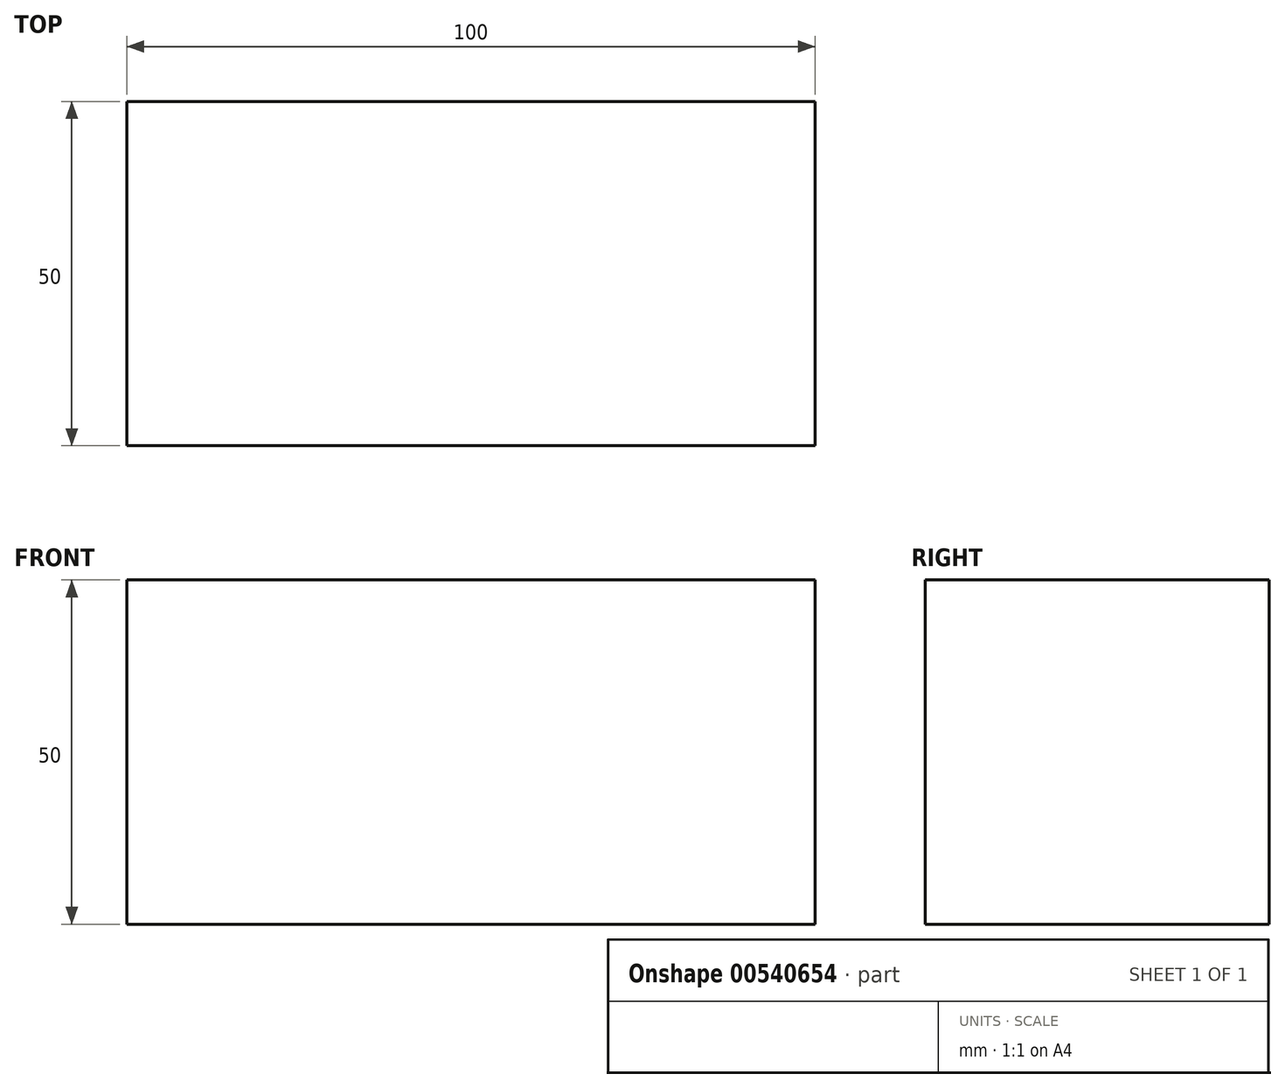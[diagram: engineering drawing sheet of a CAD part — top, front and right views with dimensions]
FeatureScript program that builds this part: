
annotation { "Feature Type Name" : "Feature", "Feature Type Description" : "" }
export const myFeature = defineFeature(function(context is Context, id is Id, definition is map)
    precondition{}
    {
        {
            var Q0;
            Q0=qCreatedBy(makeId("Top.planeOp"),FACE);
            var sketch = newSketch(context, id + "F0", { "sketchPlane" : qUnion([Q0])});
            skLineSegment(sketch, "E0.bottom", {"start": v(0, 0) * mm, "end": v(100, 0) * mm});
            skLineSegment(sketch, "E0.top", {"start": v(0, -50) * mm, "end": v(100, -50) * mm});
            skLineSegment(sketch, "E0.left", {"start": v(0, 0) * mm, "end": v(0, -50) * mm});
            skLineSegment(sketch, "E0.right", {"start": v(100, 0) * mm, "end": v(100, -50) * mm});
            skSolve(sketch);
        }
        {
            var Q0;
            Q0 = qSketchRegion(id + "F0", true);
            extrude(context, id + "F1", {"entities" : qUnion([Q0]), "depth" : 50 * mm, "offsetDistance" : 25 * mm});
        }
    });
